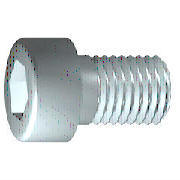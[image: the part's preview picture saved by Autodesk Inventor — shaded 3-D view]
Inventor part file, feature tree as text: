
AUTODESK INVENTOR PART (.ipt)
format: ipt  version: 2013 (Build 170138000, 138)  size: 178,176 bytes
history: native  units: mm (DEFAULTED — no unit token found)
features: sketch x2, extrude x1, plane x1, fillet x1
ambient origin geometry x7: Origin, YZ Plane, XY Plane, X Axis, Y Axis, Z Axis, Center Point
bodies: Solid1 (feature_tree), Body (feature_tree)
feature tree (5):
  extrude  "Slot"  Depth=0.306825mm
  plane  "Work Plane1"
  fillet  "Fillet2"  Radius=3.0mm
  sketch  "Sketch1"  dims[d1=18.0mm d2=0.306825mm d3=3.0mm]
  sketch  "Sketch2"  dims[d4=1.5mm d5=60.0deg d6=3.0mm d7=3.0mm d8=2.886751mm d9=5.5mm d10=90.0deg d11=10.0mm d12=0.0mm d13=18.0mm d14=0.0mm d15=0.306725mm d16=0.306725mm d17=0.3mm d19=0.0mm d26=45.0mm d27=45.0deg d28=0.0mm d29=0.0mm d30=0.1mm]
